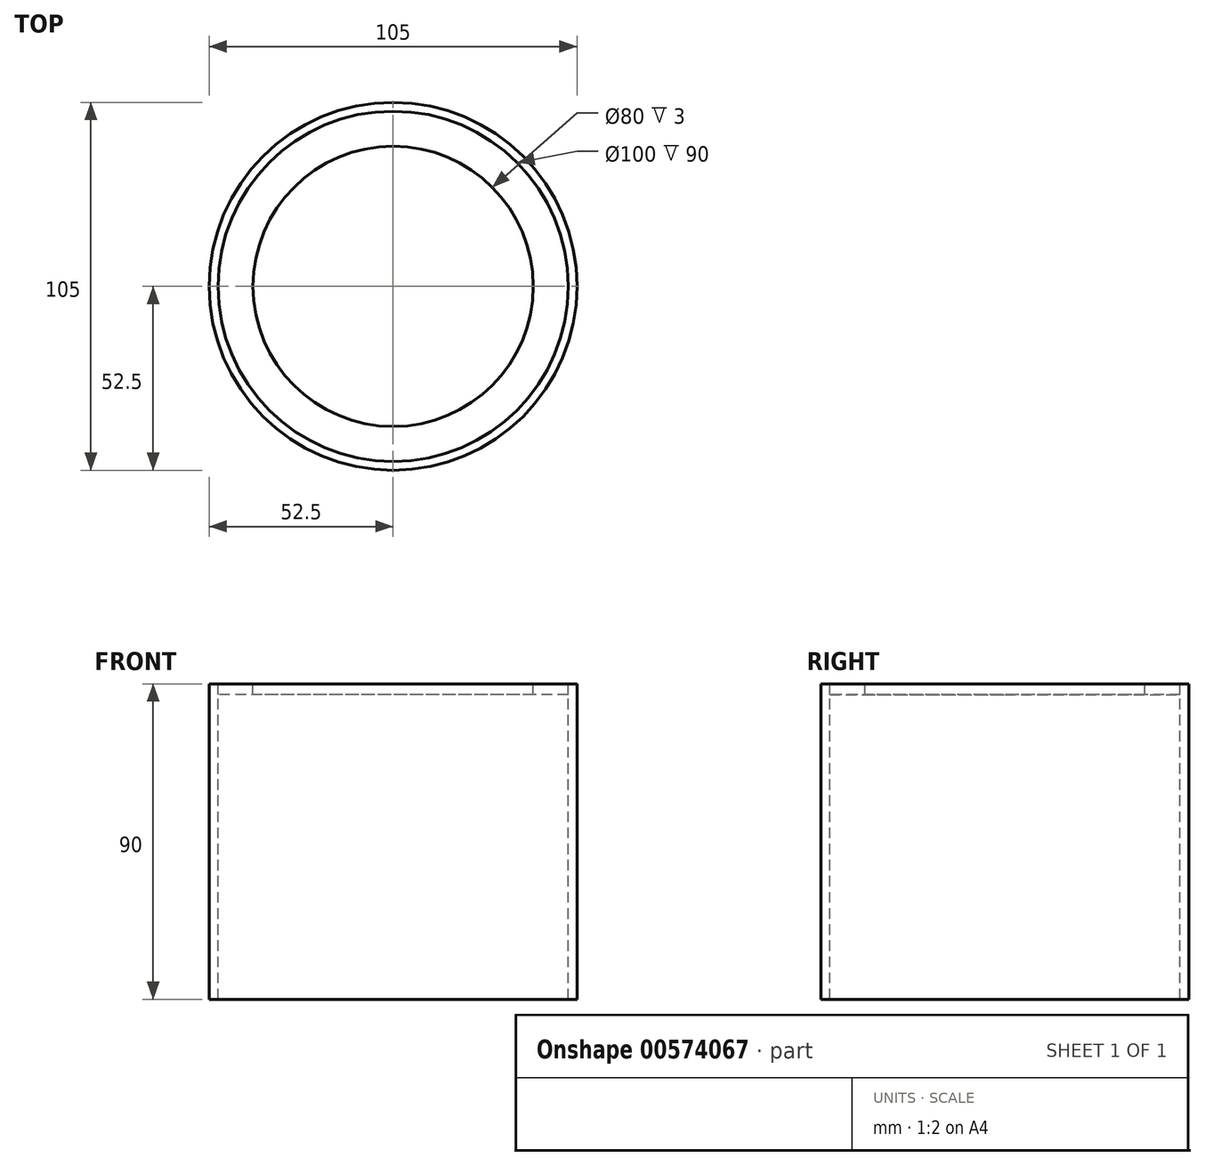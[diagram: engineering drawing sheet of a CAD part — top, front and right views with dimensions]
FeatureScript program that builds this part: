
annotation { "Feature Type Name" : "Feature", "Feature Type Description" : "" }
export const myFeature = defineFeature(function(context is Context, id is Id, definition is map)
    precondition{}
    {
        {
            var Q0;
            Q0=qCreatedBy(makeId("Top.planeOp"),FACE);
            var sketch = newSketch(context, id + "F0", { "sketchPlane" : qUnion([Q0])});
            skCircle(sketch, "E0", {"center": v(0, 0) * mm, "radius": 50 * mm});
            skCircle(sketch, "E1", {"center": v(0, 0) * mm, "radius": 52.5 * mm});
            skSolve(sketch);
        }
        {
            var Q0;
            Q0=makeQuery(id+"F0.imprint","IMPRINT",FACE,{"disambiguationData":[TD([[makeQuery(id+"F0.imprint","IMPRINT",EDGE,{"derivedFrom":sQuery(id+"F0.wireOp",EDGE,"E0")}),-1.0]])]});
            extrude(context, id + "F1", {"entities" : qUnion([Q0]), "oppositeDirection" : true, "depth" : 90 * mm, "offsetDistance" : 25 * mm});
        }
        {
            var Q0;
            Q0=qCreatedBy(makeId("Top.planeOp"),FACE);
            var sketch = newSketch(context, id + "F2", { "sketchPlane" : qUnion([Q0])});
            skCircle(sketch, "E2", {"center": v(0, 0) * mm, "radius": 50 * mm});
            skCircle(sketch, "E3", {"center": v(0, 0) * mm, "radius": 40 * mm});
            skSolve(sketch);
        }
        {
            var Q0;
            Q0 = qSketchRegion(id + "F2", true);
            extrude(context, id + "F3", {"entities" : qUnion([Q0]), "oppositeDirection" : true, "depth" : 3 * mm, "offsetDistance" : 25 * mm});
        }
    });
